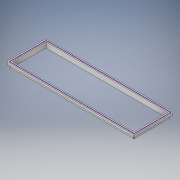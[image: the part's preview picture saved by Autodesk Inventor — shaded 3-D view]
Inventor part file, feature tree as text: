
AUTODESK INVENTOR PART (.ipt)
format: ipt  version: 2019 (Build 230136000, 136)  size: 182,784 bytes
history: native  units: mm
features: sketch x6, extrude x4, fillet x2
ambient origin geometry x8: Origin, YZ Plane, XZ Plane, XY Plane, X Axis, Y Axis, Z Axis, Center Point
bodies: Solid1 (feature_tree)
feature tree (12):
  extrude  "Extrusion1"  Depth=51.0mm
  sketch  "Sketch2"  dims[d2=187.0mm d3=55.0mm]
  sketch  "Sketch3"  dims[d4=8.0mm d5=0.0mm d6=191.0mm]
  sketch  "Sketch4"  dims[d7=59.0mm d8=2.0mm d9=2.0mm d10=4.0mm d11=0.0mm]
  extrude  "Extrusion2"  Depth=55.0mm
  extrude  "Extrusion3"  Depth=191.0mm
  extrude  "Extrusion4"  Depth=2.0mm
  fillet  "Fillet1"  Radius=2.0mm
  fillet  "Fillet2"  Radius=4.0mm
  sketch  "Sketch1"  dims[d0=183.0mm d1=51.0mm]
  sketch  "Sketch5"  dims[d12=191.0mm]
  sketch  "Sketch6"  dims[d13=59.0mm d14=4.0mm d15=0.0mm d16=4.0mm d17=0.0mm d18=1.0mm d19=1.0mm]
